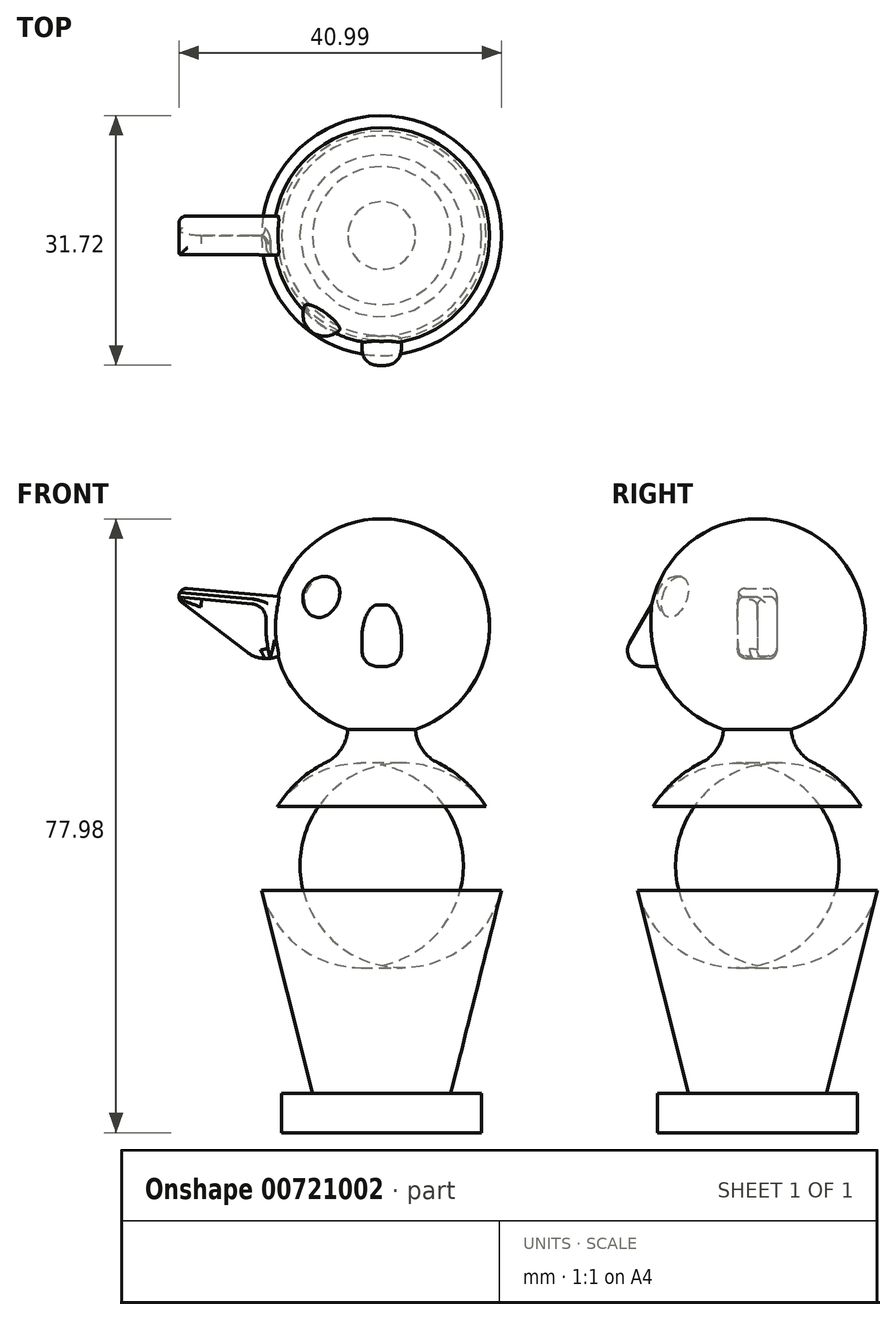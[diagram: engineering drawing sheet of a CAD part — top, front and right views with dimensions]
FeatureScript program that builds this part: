
annotation { "Feature Type Name" : "Feature", "Feature Type Description" : "" }
export const myFeature = defineFeature(function(context is Context, id is Id, definition is map)
    precondition{}
    {
        {
            var Q0;
            Q0=qCreatedBy(makeId("Front.planeOp"),FACE);
            var sketch = newSketch(context, id + "F0", { "sketchPlane" : qUnion([Q0])});
            skLineSegment(sketch, "E0", {"start": v(0, -32.27) * mm, "end": v(-8.6, -32.27) * mm});
            skLineSegment(sketch, "E1", {"start": v(-8.6, -32.27) * mm, "end": v(-16.69, 0) * mm});
            skLineSegment(sketch, "E2", {"start": v(-16.69, 0) * mm, "end": v(-8.6, 11.48) * mm});
            skLineSegment(sketch, "E3", {"start": v(-8.6, 11.48) * mm, "end": v(-4.3, 11.48) * mm});
            skArc(sketch, "E4", {"start": v(0, 41.4) * mm, "mid": v(-13.54, 29.86) * mm, "end": v(-4.3, 14.66) * mm});
            skLineSegment(sketch, "E5", {"start": v(-4.3, 11.48) * mm, "end": v(-4.3, 14.66) * mm});
            skLineSegment(sketch, "E6", {"start": v(0, -32.27) * mm, "end": v(0, 41.4) * mm});
            skPoint(sketch, "E7.orphan", {"position": v(0, 11.48) * mm});
            skSolve(sketch);
        }
        {
            var Q0;
            Q0=makeQuery(id+"F0.imprint","IMPRINT",FACE,{"disambiguationData":[TD([[makeQuery(id+"F0.imprint","IMPRINT",EDGE,{"derivedFrom":sQuery(id+"F0.wireOp",EDGE,"E0")}),-1.0]])]});
            var Q1;
            Q1=sQuery(id+"F0.wireOp",EDGE,"E6");
            revolve(context, id + "F1", {"entities" : qUnion([Q0]), "axis" : qUnion([Q1]), "revolveType" : RevolveType.FULL});
        }
        {
            var Q0;
            Q0=makeQuery(id+"F1.opRevolve","SWEPT_EDGE",EDGE,{"disambiguationData":[OSD([sQuery(id+"F0.wireOp",EDGE,"E1"),sQuery(id+"F0.wireOp",EDGE,"E2")])]});
            fillet(context, id + "F2", {"entities" : qUnion([Q0]), "radius" : 13 * mm, "tangentPropagation" : true, "allowEdgeOverflow" : false});
        }
        {
            var Q0;
            Q0=makeQuery(id+"F1.opRevolve","SWEPT_EDGE",EDGE,{"disambiguationData":[OSD([sQuery(id+"F0.wireOp",EDGE,"E2"),sQuery(id+"F0.wireOp",EDGE,"E3")])]});
            fillet(context, id + "F3", {"entities" : qUnion([Q0]), "radius" : 15 * mm, "tangentPropagation" : true, "allowEdgeOverflow" : false});
        }
        {
            var Q0;
            Q0=makeQuery(id+"F3.opFillet","BLEND_EDGE",EDGE,{"blendedFrom":[makeQuery(id+"F1.opRevolve","SWEPT_EDGE",EDGE,{"disambiguationData":[OSD([sQuery(id+"F0.wireOp",EDGE,"E2"),sQuery(id+"F0.wireOp",EDGE,"E3")])]}),makeQuery(id+"F1.opRevolve","SWEPT_FACE",FACE,{"disambiguationData":[OSD([sQuery(id+"F0.wireOp",EDGE,"E5")])]})],"blendedInto":[makeQuery(id+"F1.opRevolve","SWEPT_FACE",FACE,{"disambiguationData":[OSD([sQuery(id+"F0.wireOp",EDGE,"E5")])]})]});
            fillet(context, id + "F4", {"entities" : qUnion([Q0]), "radius" : 5 * mm, "tangentPropagation" : true, "allowEdgeOverflow" : false});
        }
        {
            var Q0;
            Q0=qCreatedBy(makeId("Front.planeOp"),FACE);
            var sketch = newSketch(context, id + "F5", { "sketchPlane" : qUnion([Q0])});
            skLineSegment(sketch, "E8", {"start": v(-4.64, 30.74) * mm, "end": v(-28.12, 32.86) * mm});
            skLineSegment(sketch, "E9", {"start": v(-28.12, 32.86) * mm, "end": v(-17.08, 24.46) * mm});
            skLineSegment(sketch, "E10", {"start": v(-12.11, 24.56) * mm, "end": v(-4.64, 30.74) * mm});
            skPoint(sketch, "E11.visualSharp", {"position": v(-14.56, 22.53) * mm});
            skArc(sketch, "E11.filletArc", {"start": v(-17.08, 24.46) * mm, "mid": v(-14.58, 23.64) * mm, "end": v(-12.11, 24.56) * mm});
            skSolve(sketch);
        }
        {
            var Q0;
            Q0=makeQuery(id+"F5.imprint","IMPRINT",FACE,{"disambiguationData":[TD([[makeQuery(id+"F5.imprint","IMPRINT",EDGE,{"derivedFrom":sQuery(id+"F5.wireOp",EDGE,"E8")}),1.0]])]});
            extrude(context, id + "F6", {"entities" : qUnion([Q0]), "operationType" : NewBodyOperationType.ADD, "depth" : 2.5 * mm, "hasSecondDirection" : true, "secondDirectionOppositeDirection" : true, "secondDirectionDepth" : 2.5 * mm});
        }
        {
            var Q0;
            Q0=qCreatedBy(makeId("Right.planeOp"),FACE);
            var sketch = newSketch(context, id + "F7", { "sketchPlane" : qUnion([Q0])});
            skLineSegment(sketch, "E12", {"start": v(-12.25, 32.5) * mm, "end": v(-17.95, 22.64) * mm});
            skLineSegment(sketch, "E13", {"start": v(-17.95, 22.64) * mm, "end": v(-10.28, 22.64) * mm});
            skLineSegment(sketch, "E14", {"start": v(-10.28, 22.64) * mm, "end": v(-12.25, 32.5) * mm});
            skSolve(sketch);
        }
        {
            var Q0;
            Q0=qSketchRegion(id+"F7",true);
            extrude(context, id + "F8", {"entities" : qUnion([Q0]), "operationType" : NewBodyOperationType.ADD, "depth" : 2.5 * mm, "hasSecondDirection" : true, "secondDirectionOppositeDirection" : true, "secondDirectionDepth" : 2.5 * mm});
        }
        {
            var Q0;
            Q0=makeQuery(id+"F8.opExtrude","CAP_EDGE",EDGE,{"disambiguationData":[OSD([sQuery(id+"F7.wireOp",EDGE,"E12")])],"isStart":true});
            var Q1;
            Q1=makeQuery(id+"F8.opExtrude","CAP_EDGE",EDGE,{"disambiguationData":[OSD([sQuery(id+"F7.wireOp",EDGE,"E12")])],"isStart":false});
            var Q2;
            Q2=makeQuery(id+"F8.opExtrude","SWEPT_EDGE",EDGE,{"disambiguationData":[OSD([sQuery(id+"F7.wireOp",EDGE,"E12"),sQuery(id+"F7.wireOp",EDGE,"E13")])]});
            var Q3;
            Q3=makeQuery(id+"F8.opExtrude","CAP_EDGE",EDGE,{"disambiguationData":[OSD([sQuery(id+"F7.wireOp",EDGE,"E13")])],"isStart":true});
            var Q4;
            Q4=makeQuery(id+"F8.opExtrude","CAP_EDGE",EDGE,{"disambiguationData":[OSD([sQuery(id+"F7.wireOp",EDGE,"E13")])],"isStart":false});
            fillet(context, id + "F9", {"entities" : qUnion([Q0, Q1, Q2, Q3, Q4]), "radius" : 2 * mm, "tangentPropagation" : true, "allowEdgeOverflow" : false});
        }
        {
            var Q0;
            Q0=makeQuery(id+"F6.opExtrude","CAP_FACE",FACE,{"disambiguationData":[OSD([sQuery(id+"F5.wireOp",EDGE,"E8"),sQuery(id+"F5.wireOp",EDGE,"E9"),sQuery(id+"F5.wireOp",EDGE,"E10"),sQuery(id+"F5.wireOp",EDGE,"E11.filletArc")])],"isStart":false});
            var sketch = newSketch(context, id + "F10", { "sketchPlane" : qUnion([Q0])});
            skLineSegment(sketch, "E15.0", {"start": v(-14.43, 30.42) * mm, "end": v(-28.23, 31.67) * mm});
            skArc(sketch, "E15.1", {"start": v(-14.43, 30.42) * mm, "mid": v(-14.67, 27.03) * mm, "end": v(-14.13, 23.68) * mm});
            skLineSegment(sketch, "E16", {"start": v(-14.13, 23.68) * mm, "end": v(-14.5, 22.11) * mm});
            skLineSegment(sketch, "E17", {"start": v(-14.5, 22.11) * mm, "end": v(-28.23, 31.67) * mm});
            skSolve(sketch);
        }
        {
            var Q0;
            Q0=qSketchRegion(id+"F10",true);
            extrude(context, id + "F11", {"entities" : qUnion([Q0]), "operationType" : NewBodyOperationType.REMOVE, "oppositeDirection" : true, "depth" : 2.5 * mm});
        }
        {
            var Q0;
            Q0=makeQuery(id+"F11.boolean.opBoolean","INTERSECT",EDGE,{"derivedFrom":[makeQuery(id+"F6.opExtrude","SWEPT_FACE",FACE,{"disambiguationData":[OSD([sQuery(id+"F5.wireOp",EDGE,"E9")])]}),makeQuery(id+"F11.opExtrude","SWEPT_FACE",FACE,{"disambiguationData":[OSD([sQuery(id+"F10.wireOp",EDGE,"E15.0")])]})]});
            var Q1;
            Q1=makeQuery(id+"F11.boolean.opBoolean","COPY",EDGE,{"derivedFrom":makeQuery(id+"F11.opExtrude","SWEPT_EDGE",EDGE,{"disambiguationData":[OSD([sQuery(id+"F10.wireOp",EDGE,"E15.0"),sQuery(id+"F10.wireOp",EDGE,"E15.1")])]})});
            fillet(context, id + "F12", {"entities" : qUnion([Q0, Q1]), "radius" : 2 * mm, "tangentPropagation" : true, "allowEdgeOverflow" : false});
        }
        {
            var Q0;
            Q0=makeQuery(id+"F11.boolean.opBoolean","INTERSECT",EDGE,{"derivedFrom":[makeQuery(id+"F6.opExtrude","SWEPT_FACE",FACE,{"disambiguationData":[OSD([sQuery(id+"F5.wireOp",EDGE,"E9")])]}),makeQuery(id+"F11.opExtrude","CAP_FACE",FACE,{"disambiguationData":[OSD([sQuery(id+"F10.wireOp",EDGE,"E15.0"),sQuery(id+"F10.wireOp",EDGE,"E15.1"),sQuery(id+"F10.wireOp",EDGE,"E16"),sQuery(id+"F10.wireOp",EDGE,"E17")])],"isStart":false})]});
            var Q1;
            Q1=makeQuery(id+"F6.opExtrude","CAP_EDGE",EDGE,{"disambiguationData":[OSD([sQuery(id+"F5.wireOp",EDGE,"E9")])],"isStart":true});
            var Q2;
            Q2=makeQuery(id+"F6.opExtrude","CAP_EDGE",EDGE,{"disambiguationData":[OSD([sQuery(id+"F5.wireOp",EDGE,"E8")])],"isStart":false});
            var Q3;
            Q3=makeQuery(id+"F6.opExtrude","CAP_EDGE",EDGE,{"disambiguationData":[OSD([sQuery(id+"F5.wireOp",EDGE,"E8")])],"isStart":true});
            var Q4;
            Q4=makeQuery(id+"F6.opExtrude","SWEPT_EDGE",EDGE,{"disambiguationData":[OSD([sQuery(id+"F5.wireOp",EDGE,"E8"),sQuery(id+"F5.wireOp",EDGE,"E9")])]});
            fillet(context, id + "F13", {"entities" : qUnion([Q0, Q1, Q2, Q3, Q4]), "radius" : 1 * mm, "tangentPropagation" : true, "allowEdgeOverflow" : false});
        }
        {
            var Q0;
            Q0=makeQuery(id+"F11.boolean.opBoolean","COPY",EDGE,{"derivedFrom":makeQuery(id+"F11.opExtrude","CAP_EDGE",EDGE,{"disambiguationData":[OSD([sQuery(id+"F10.wireOp",EDGE,"E15.0")])],"isStart":false})});
            var Q1;
            {var subQ0=sQuery(id+"F10.wireOp",EDGE,"E15.1");var subQ1=sQuery(id+"F10.wireOp",EDGE,"E15.0");Q1=makeQuery(id+"F12.opFillet","BLEND_EDGE",EDGE,{"blendedFrom":[makeQuery(id+"F11.boolean.opBoolean","COPY",EDGE,{"derivedFrom":makeQuery(id+"F11.opExtrude","SWEPT_EDGE",EDGE,{"disambiguationData":[OSD([subQ1,subQ0])]})}),makeQuery(id+"F11.boolean.opBoolean","COPY",FACE,{"derivedFrom":makeQuery(id+"F11.opExtrude","CAP_FACE",FACE,{"disambiguationData":[OSD([subQ1,subQ0,sQuery(id+"F10.wireOp",EDGE,"E16"),sQuery(id+"F10.wireOp",EDGE,"E17")])],"isStart":false})})],"blendedInto":[makeQuery(id+"F11.boolean.opBoolean","COPY",FACE,{"derivedFrom":makeQuery(id+"F11.opExtrude","CAP_FACE",FACE,{"disambiguationData":[OSD([subQ1,subQ0,sQuery(id+"F10.wireOp",EDGE,"E16"),sQuery(id+"F10.wireOp",EDGE,"E17")])],"isStart":false})})]});}
            var Q2;
            Q2=makeQuery(id+"F11.boolean.opBoolean","COPY",EDGE,{"derivedFrom":makeQuery(id+"F11.opExtrude","CAP_EDGE",EDGE,{"disambiguationData":[OSD([sQuery(id+"F10.wireOp",EDGE,"E15.1")])],"isStart":false})});
            var Q3;
            Q3=makeQuery(id+"F12.opFillet","BLEND_EDGE",EDGE,{"blendedFrom":[makeQuery(id+"F11.boolean.opBoolean","COPY",EDGE,{"derivedFrom":makeQuery(id+"F11.opExtrude","SWEPT_EDGE",EDGE,{"disambiguationData":[OSD([sQuery(id+"F10.wireOp",EDGE,"E15.0"),sQuery(id+"F10.wireOp",EDGE,"E15.1")])]})}),makeQuery(id+"F6.opExtrude","CAP_FACE",FACE,{"disambiguationData":[OSD([sQuery(id+"F5.wireOp",EDGE,"E8"),sQuery(id+"F5.wireOp",EDGE,"E9"),sQuery(id+"F5.wireOp",EDGE,"E10"),sQuery(id+"F5.wireOp",EDGE,"E11.filletArc")])],"isStart":false})],"blendedInto":[makeQuery(id+"F6.opExtrude","CAP_FACE",FACE,{"disambiguationData":[OSD([sQuery(id+"F5.wireOp",EDGE,"E8"),sQuery(id+"F5.wireOp",EDGE,"E9"),sQuery(id+"F5.wireOp",EDGE,"E10"),sQuery(id+"F5.wireOp",EDGE,"E11.filletArc")])],"isStart":false})]});
            fillet(context, id + "F14", {"entities" : qUnion([Q0, Q1, Q2, Q3]), "radius" : 1 * mm, "tangentPropagation" : true, "allowEdgeOverflow" : false});
        }
        {
            var Q0;
            Q0=makeQuery(id+"F6.opExtrude","CAP_EDGE",EDGE,{"disambiguationData":[OSD([sQuery(id+"F5.wireOp",EDGE,"E11.filletArc")])],"isStart":false});
            fillet(context, id + "F15", {"entities" : qUnion([Q0]), "radius" : 1 * mm, "tangentPropagation" : true, "allowEdgeOverflow" : false});
        }
        {
            var Q0;
            Q0=qCreatedBy(makeId("Front.planeOp"),FACE);
            cPlane(context, id + "F16", {"entities" : qUnion([Q0]), "cplaneType" : CPlaneType.OFFSET, "offset" : 10 * mm, "width" : 150 * mm, "height" : 150 * mm});
        }
        {
            var Q0;
            Q0=qCreatedBy(id+"F16.planeOp",FACE);
            var sketch = newSketch(context, id + "F17", { "sketchPlane" : qUnion([Q0])});
            skArc(sketch, "E18", {"start": v(-7.23, 28.53) * mm, "mid": v(-4.45, 31.3) * mm, "end": v(-7.23, 34.08) * mm});
            skLineSegment(sketch, "E19", {"start": v(-7.23, 34.08) * mm, "end": v(-7.23, 28.53) * mm});
            skSolve(sketch);
        }
        {
            var Q0;
            Q0=qSketchRegion(id+"F17",true);
            var Q1;
            Q1=sQuery(id+"F17.wireOp",EDGE,"E19");
            revolve(context, id + "F18", {"operationType" : NewBodyOperationType.ADD, "entities" : qUnion([Q0]), "axis" : qUnion([Q1]), "revolveType" : RevolveType.FULL});
        }
        {
            var Q0;
            Q0=qCreatedBy(makeId("Front.planeOp"),FACE);
            var sketch = newSketch(context, id + "F19", { "sketchPlane" : qUnion([Q0])});
            skLineSegment(sketch, "E20.bottom", {"start": v(0, -31.58) * mm, "end": v(-12.7, -31.58) * mm});
            skLineSegment(sketch, "E20.top", {"start": v(0, -36.58) * mm, "end": v(-12.7, -36.58) * mm});
            skLineSegment(sketch, "E20.left", {"start": v(0, -31.58) * mm, "end": v(0, -36.58) * mm});
            skLineSegment(sketch, "E20.right", {"start": v(-12.7, -31.58) * mm, "end": v(-12.7, -36.58) * mm});
            skSolve(sketch);
        }
        {
            var Q0;
            Q0=makeQuery(id+"F19.imprint","IMPRINT",FACE,{"disambiguationData":[TD([[makeQuery(id+"F19.imprint","IMPRINT",EDGE,{"derivedFrom":sQuery(id+"F19.wireOp",EDGE,"E20.bottom")}),1.0]])]});
            var Q1;
            Q1=sQuery(id+"F19.wireOp",EDGE,"E20.left");
            revolve(context, id + "F20", {"operationType" : NewBodyOperationType.ADD, "entities" : qUnion([Q0]), "axis" : qUnion([Q1]), "revolveType" : RevolveType.FULL});
        }
    });
